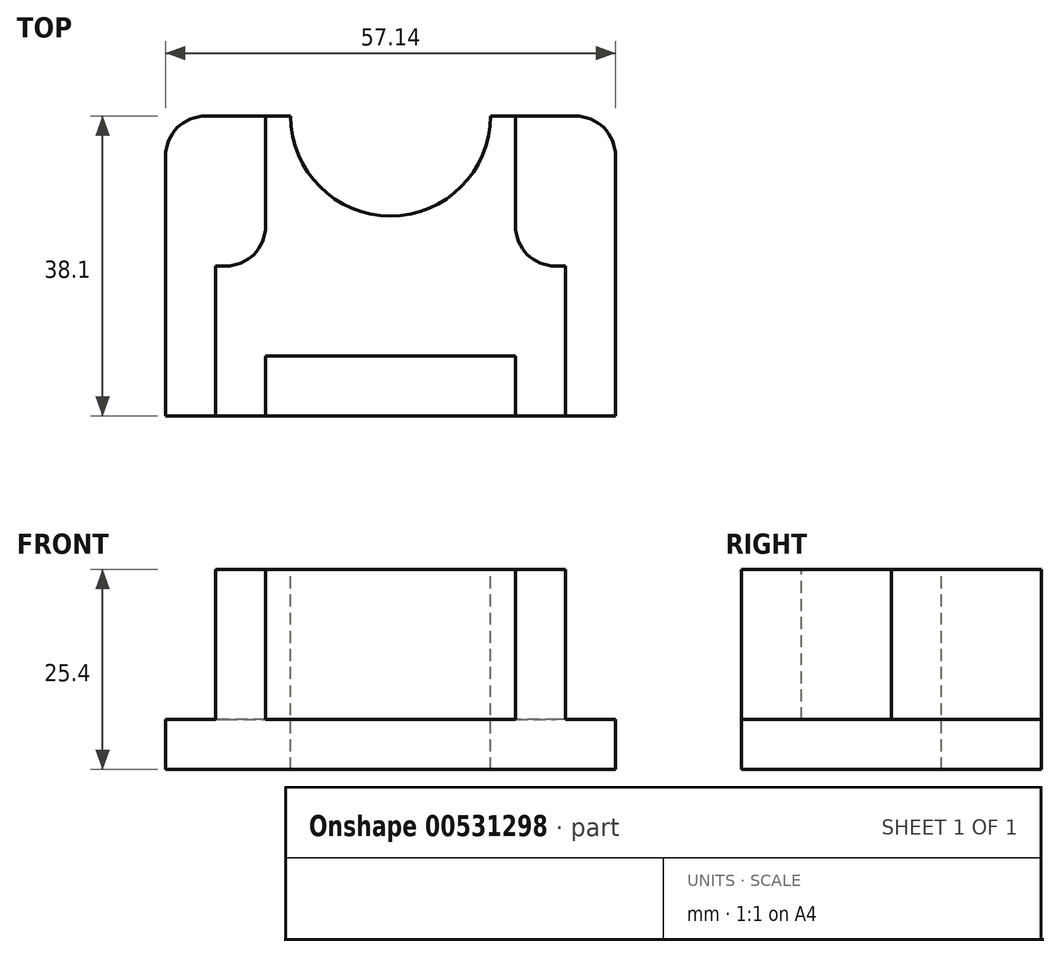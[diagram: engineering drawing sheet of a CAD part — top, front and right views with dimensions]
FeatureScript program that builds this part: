
annotation { "Feature Type Name" : "Feature", "Feature Type Description" : "" }
export const myFeature = defineFeature(function(context is Context, id is Id, definition is map)
    precondition{}
    {
        {
            var Q0;
            Q0=qCreatedBy(makeId("Top.planeOp"),FACE);
            var sketch = newSketch(context, id + "F0", { "sketchPlane" : qUnion([Q0])});
            skLineSegment(sketch, "E0.bottom", {"start": v(28.58, 19.05) * mm, "end": v(-28.57, 19.05) * mm});
            skLineSegment(sketch, "E0.top", {"start": v(28.57, -19.05) * mm, "end": v(-28.58, -19.05) * mm});
            skLineSegment(sketch, "E0.left", {"start": v(28.58, 19.05) * mm, "end": v(28.57, -19.05) * mm});
            skLineSegment(sketch, "E0.right", {"start": v(-28.57, 19.05) * mm, "end": v(-28.58, -19.05) * mm});
            skPoint(sketch, "E0.middle", {"position": v(0, 0) * mm});
            skSolve(sketch);
        }
        {
            var Q0;
            Q0 = qSketchRegion(id + "F0", true);
            extrude(context, id + "F1", {"entities" : qUnion([Q0]), "depth" : 25.4 * mm, "offsetDistance" : 25.4 * mm});
        }
        {
            var Q0;
            Q0=makeQuery(id+"F1.opExtrude","CAP_FACE",FACE,{"disambiguationData":[OSD([sQuery(id+"F0.wireOp",EDGE,"E0.bottom"),sQuery(id+"F0.wireOp",EDGE,"E0.top"),sQuery(id+"F0.wireOp",EDGE,"E0.left"),sQuery(id+"F0.wireOp",EDGE,"E0.right")])],"isStart":false});
            var sketch = newSketch(context, id + "F2", { "sketchPlane" : qUnion([Q0])});
            skLineSegment(sketch, "E1.bottom", {"start": v(-15.88, -19.05) * mm, "end": v(0, -19.05) * mm});
            skLineSegment(sketch, "E1.top", {"start": v(-15.88, -11.43) * mm, "end": v(0, -11.43) * mm});
            skLineSegment(sketch, "E1.left", {"start": v(-15.88, -19.05) * mm, "end": v(-15.88, -11.43) * mm});
            skLineSegment(sketch, "E2.bottom", {"start": v(-28.58, -19.05) * mm, "end": v(-22.23, -19.05) * mm});
            skLineSegment(sketch, "E2.top", {"start": v(-28.58, 19.05) * mm, "end": v(-22.23, 19.05) * mm});
            skLineSegment(sketch, "E2.left", {"start": v(-28.58, -19.05) * mm, "end": v(-28.58, 19.05) * mm});
            skLineSegment(sketch, "E2.right", {"start": v(-22.23, -19.05) * mm, "end": v(-22.23, 0) * mm});
            skLineSegment(sketch, "E3.bottom", {"start": v(-22.23, 19.05) * mm, "end": v(-15.88, 19.05) * mm});
            skLineSegment(sketch, "E3.top", {"start": v(-22.23, 0) * mm, "end": v(-15.88, 0) * mm});
            skLineSegment(sketch, "E3.right", {"start": v(-15.88, 19.05) * mm, "end": v(-15.88, 0) * mm});
            skLineSegment(sketch, "E4", {"start": v(0, -11.43) * mm, "end": v(0, -19.05) * mm});
            skLineSegment(sketch, "E5.MirrorCS", {"start": v(-28.58, 57.15) * mm, "end": v(-28.58, 19.05) * mm});
            skLineSegment(sketch, "E6.MirrorCS", {"start": v(-22.23, 57.15) * mm, "end": v(-22.23, 19.05) * mm});
            skLineSegment(sketch, "E7.MirrorCS", {"start": v(15.88, 19.05) * mm, "end": v(15.88, 0) * mm});
            skLineSegment(sketch, "E8.MirrorCS", {"start": v(22.23, 19.05) * mm, "end": v(15.88, 19.05) * mm});
            skLineSegment(sketch, "E9.MirrorCS", {"start": v(28.58, 19.05) * mm, "end": v(22.23, 19.05) * mm});
            skLineSegment(sketch, "E10.MirrorCS", {"start": v(28.58, -19.05) * mm, "end": v(28.58, 19.05) * mm});
            skLineSegment(sketch, "E11.MirrorCS", {"start": v(22.23, -19.05) * mm, "end": v(22.23, 0) * mm});
            skLineSegment(sketch, "E12.MirrorCS", {"start": v(28.58, -19.05) * mm, "end": v(22.23, -19.05) * mm});
            skLineSegment(sketch, "E13.MirrorCS", {"start": v(15.88, -19.05) * mm, "end": v(15.88, -11.43) * mm});
            skLineSegment(sketch, "E14.MirrorCS", {"start": v(15.88, -11.43) * mm, "end": v(0, -11.43) * mm});
            skLineSegment(sketch, "E15.MirrorCS", {"start": v(15.88, -19.05) * mm, "end": v(0, -19.05) * mm});
            skLineSegment(sketch, "E16.MirrorCS", {"start": v(22.23, 0) * mm, "end": v(15.88, 0) * mm});
            skSolve(sketch);
        }
        {
            var Q0;
            Q0 = qSketchRegion(id + "F2", true);
            extrude(context, id + "F3", {"entities" : qUnion([Q0]), "operationType" : NewBodyOperationType.REMOVE, "oppositeDirection" : true, "depth" : 19.05 * mm, "offsetDistance" : 25.4 * mm});
        }
        {
            var Q0;
            Q0=makeQuery(id+"F1.opExtrude","CAP_FACE",FACE,{"disambiguationData":[OSD([sQuery(id+"F0.wireOp",EDGE,"E0.bottom"),sQuery(id+"F0.wireOp",EDGE,"E0.top"),sQuery(id+"F0.wireOp",EDGE,"E0.left"),sQuery(id+"F0.wireOp",EDGE,"E0.right")])],"isStart":false});
            var sketch = newSketch(context, id + "F4", { "sketchPlane" : qUnion([Q0])});
            skCircle(sketch, "E17", {"center": v(0, 19.05) * mm, "radius": 12.7 * mm});
            skSolve(sketch);
        }
        {
            var Q0;
            Q0 = qSketchRegion(id + "F4", true);
            extrude(context, id + "F5", {"entities" : qUnion([Q0]), "operationType" : NewBodyOperationType.REMOVE, "endBound" : BoundingType.THROUGH_ALL, "oppositeDirection" : true, "depth" : 25.4 * mm, "offsetDistance" : 25.4 * mm});
        }
        {
            var Q0;
            Q0=makeQuery(id+"F3.boolean.opBoolean","COPY",EDGE,{"derivedFrom":makeQuery(id+"F3.opExtrude","SWEPT_EDGE",EDGE,{"disambiguationData":[OSD([sQuery(id+"F2.wireOp",EDGE,"E3.top"),sQuery(id+"F2.wireOp",EDGE,"E3.right")])]})});
            var Q1;
            Q1=makeQuery(id+"F3.boolean.opBoolean","COPY",EDGE,{"derivedFrom":makeQuery(id+"F3.opExtrude","SWEPT_EDGE",EDGE,{"disambiguationData":[OSD([sQuery(id+"F2.wireOp",EDGE,"E7.MirrorCS"),sQuery(id+"F2.wireOp",EDGE,"E16.MirrorCS")])]})});
            fillet(context, id + "F6", {"entities" : qUnion([Q0, Q1]), "radius" : 5.08 * mm, "tangentPropagation" : true, "allowEdgeOverflow" : false});
        }
        {
            var Q0;
            Q0=makeQuery(id+"F1.opExtrude","SWEPT_EDGE",EDGE,{"disambiguationData":[OSD([sQuery(id+"F0.wireOp",EDGE,"E0.bottom"),sQuery(id+"F0.wireOp",EDGE,"E0.left")])]});
            var Q1;
            Q1=makeQuery(id+"F1.opExtrude","SWEPT_EDGE",EDGE,{"disambiguationData":[OSD([sQuery(id+"F0.wireOp",EDGE,"E0.bottom"),sQuery(id+"F0.wireOp",EDGE,"E0.right")])]});
            fillet(context, id + "F7", {"entities" : qUnion([Q0, Q1]), "radius" : 5.08 * mm, "tangentPropagation" : true, "allowEdgeOverflow" : false});
        }
    });
